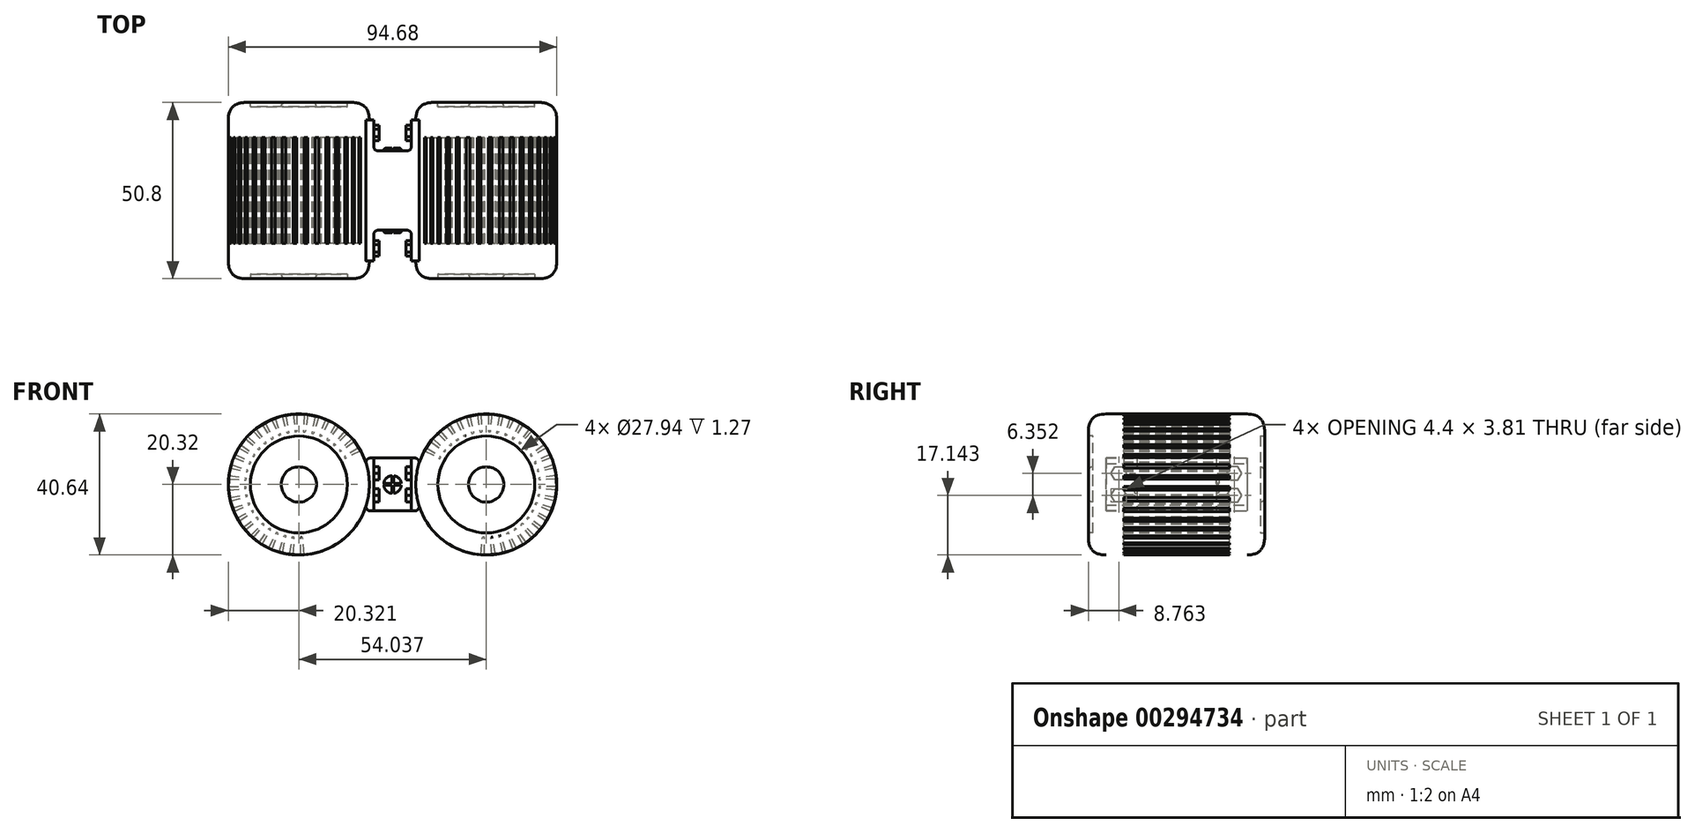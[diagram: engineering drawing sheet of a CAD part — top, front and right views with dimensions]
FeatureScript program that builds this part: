
annotation { "Feature Type Name" : "Feature", "Feature Type Description" : "" }
export const myFeature = defineFeature(function(context is Context, id is Id, definition is map)
    precondition{}
    {
        {
            var Q0;
            Q0=qCreatedBy(makeId("Front.planeOp"),FACE);
            var sketch = newSketch(context, id + "F0", { "sketchPlane" : qUnion([Q0])});
            skArc(sketch, "E0", {"start": v(26.53, 38.5) * mm, "mid": v(31.42, 78.66) * mm, "end": v(18.88, 40.2) * mm});
            skCircle(sketch, "E1", {"center": v(-27.02, 58.82) * mm, "radius": 20.32 * mm});
            skArc(sketch, "E2", {"start": v(18.88, 40.2) * mm, "mid": v(22.62, 38.98) * mm, "end": v(26.53, 38.5) * mm});
            skSolve(sketch);
        }
        {
            var Q0;
            Q0=qSketchRegion(id+"F0",true);
            extrude(context, id + "F1", {"entities" : qUnion([Q0]), "endBound" : BoundingType.SYMMETRIC, "depth" : 50.8 * mm});
        }
        {
            var Q0;
            Q0=qCreatedBy(makeId("Front.planeOp"),FACE);
            var sketch = newSketch(context, id + "F2", { "sketchPlane" : qUnion([Q0])});
            skLineSegment(sketch, "E3.1.0", {"start": v(13.83, 74.28) * mm, "end": v(17.03, 70.33) * mm});
            skLineSegment(sketch, "E3.1.1", {"start": v(13.07, 73.6) * mm, "end": v(16.65, 69.99) * mm});
            skLineSegment(sketch, "E3.1.2", {"start": v(13.07, 73.6) * mm, "end": v(13.83, 74.28) * mm});
            skLineSegment(sketch, "E3.1.3", {"start": v(16.65, 69.99) * mm, "end": v(17.03, 70.33) * mm, "construction": true});
            skLineSegment(sketch, "E3.1.4", {"start": v(16.65, 69.99) * mm, "end": v(17.03, 70.33) * mm});
            skPoint(sketch, "E4", {"position": v(27.02, 58.82) * mm});
            skPoint(sketch, "E5", {"position": v(-27.02, 58.82) * mm});
            skLineSegment(sketch, "E6", {"start": v(27.02, 58.82) * mm, "end": v(13.45, 73.94) * mm, "construction": true});
            skLineSegment(sketch, "E7.1.0", {"start": v(-13.07, 73.6) * mm, "end": v(-16.65, 69.99) * mm});
            skLineSegment(sketch, "E7.1.1", {"start": v(-13.83, 74.28) * mm, "end": v(-17.03, 70.33) * mm});
            skLineSegment(sketch, "E7.1.2", {"start": v(-13.83, 74.28) * mm, "end": v(-13.07, 73.6) * mm});
            skLineSegment(sketch, "E7.1.3", {"start": v(-17.03, 70.33) * mm, "end": v(-16.65, 69.99) * mm, "construction": true});
            skLineSegment(sketch, "E7.1.4", {"start": v(-17.03, 70.33) * mm, "end": v(-16.65, 69.99) * mm});
            skLineSegment(sketch, "E8", {"start": v(-27.02, 58.82) * mm, "end": v(-13.45, 73.94) * mm, "construction": true});
            skLineSegment(sketch, "E9.1.0", {"start": v(11.57, 72.03) * mm, "end": v(15.35, 68.63) * mm});
            skLineSegment(sketch, "E9.1.1", {"start": v(10.93, 71.24) * mm, "end": v(15.03, 68.23) * mm});
            skLineSegment(sketch, "E9.1.2", {"start": v(10.93, 71.24) * mm, "end": v(11.57, 72.03) * mm});
            skLineSegment(sketch, "E9.1.3", {"start": v(15.03, 68.23) * mm, "end": v(15.35, 68.63) * mm, "construction": true});
            skLineSegment(sketch, "E9.1.4", {"start": v(15.03, 68.23) * mm, "end": v(15.35, 68.63) * mm});
            skLineSegment(sketch, "E9.2.0", {"start": v(9.7, 69.45) * mm, "end": v(13.96, 66.68) * mm});
            skLineSegment(sketch, "E9.2.1", {"start": v(9.18, 68.57) * mm, "end": v(13.7, 66.24) * mm});
            skLineSegment(sketch, "E9.2.2", {"start": v(9.18, 68.57) * mm, "end": v(9.7, 69.45) * mm});
            skLineSegment(sketch, "E9.2.3", {"start": v(13.7, 66.24) * mm, "end": v(13.96, 66.68) * mm, "construction": true});
            skLineSegment(sketch, "E9.2.4", {"start": v(13.7, 66.24) * mm, "end": v(13.96, 66.68) * mm});
            skLineSegment(sketch, "E9.15.0", {"start": v(25.41, 38.55) * mm, "end": v(25.94, 43.62) * mm});
            skLineSegment(sketch, "E9.15.1", {"start": v(26.43, 38.5) * mm, "end": v(26.45, 43.59) * mm});
            skLineSegment(sketch, "E9.15.2", {"start": v(26.43, 38.5) * mm, "end": v(25.41, 38.55) * mm});
            skLineSegment(sketch, "E9.15.3", {"start": v(26.45, 43.59) * mm, "end": v(25.94, 43.62) * mm, "construction": true});
            skLineSegment(sketch, "E9.15.4", {"start": v(26.45, 43.59) * mm, "end": v(25.94, 43.62) * mm});
            skLineSegment(sketch, "E9.16.0", {"start": v(28.6, 38.55) * mm, "end": v(28.33, 43.63) * mm});
            skLineSegment(sketch, "E9.16.1", {"start": v(29.61, 38.66) * mm, "end": v(28.84, 43.69) * mm});
            skLineSegment(sketch, "E9.16.2", {"start": v(29.61, 38.66) * mm, "end": v(28.6, 38.55) * mm});
            skLineSegment(sketch, "E9.16.3", {"start": v(28.84, 43.69) * mm, "end": v(28.33, 43.63) * mm, "construction": true});
            skLineSegment(sketch, "E9.16.4", {"start": v(28.84, 43.69) * mm, "end": v(28.33, 43.63) * mm});
            skLineSegment(sketch, "E9.17.0", {"start": v(31.75, 39.05) * mm, "end": v(30.7, 44.03) * mm});
            skLineSegment(sketch, "E9.17.1", {"start": v(32.73, 39.31) * mm, "end": v(31.18, 44.16) * mm});
            skLineSegment(sketch, "E9.17.2", {"start": v(32.73, 39.31) * mm, "end": v(31.75, 39.05) * mm});
            skLineSegment(sketch, "E9.17.3", {"start": v(31.18, 44.16) * mm, "end": v(30.7, 44.03) * mm, "construction": true});
            skLineSegment(sketch, "E9.17.4", {"start": v(31.18, 44.16) * mm, "end": v(30.7, 44.03) * mm});
            skLineSegment(sketch, "E9.18.0", {"start": v(34.79, 40.03) * mm, "end": v(32.96, 44.78) * mm});
            skLineSegment(sketch, "E9.18.1", {"start": v(35.72, 40.45) * mm, "end": v(33.42, 44.99) * mm});
            skLineSegment(sketch, "E9.18.2", {"start": v(35.72, 40.45) * mm, "end": v(34.79, 40.03) * mm});
            skLineSegment(sketch, "E9.18.3", {"start": v(33.42, 44.99) * mm, "end": v(32.96, 44.78) * mm, "construction": true});
            skLineSegment(sketch, "E9.18.4", {"start": v(33.42, 44.99) * mm, "end": v(32.96, 44.78) * mm});
            skLineSegment(sketch, "E9.19.0", {"start": v(37.63, 41.48) * mm, "end": v(35.08, 45.89) * mm});
            skLineSegment(sketch, "E9.19.1", {"start": v(38.48, 42.03) * mm, "end": v(35.5, 46.16) * mm});
            skLineSegment(sketch, "E9.19.2", {"start": v(38.48, 42.03) * mm, "end": v(37.63, 41.48) * mm});
            skLineSegment(sketch, "E9.19.3", {"start": v(35.5, 46.16) * mm, "end": v(35.08, 45.89) * mm, "construction": true});
            skLineSegment(sketch, "E9.19.4", {"start": v(35.5, 46.16) * mm, "end": v(35.08, 45.89) * mm});
            skLineSegment(sketch, "E9.20.0", {"start": v(40.21, 43.35) * mm, "end": v(37, 47.3) * mm});
            skLineSegment(sketch, "E9.20.1", {"start": v(40.97, 44.03) * mm, "end": v(37.38, 47.65) * mm});
            skLineSegment(sketch, "E9.20.2", {"start": v(40.97, 44.03) * mm, "end": v(40.21, 43.35) * mm});
            skLineSegment(sketch, "E9.20.3", {"start": v(37.38, 47.65) * mm, "end": v(37, 47.3) * mm, "construction": true});
            skLineSegment(sketch, "E9.20.4", {"start": v(37.38, 47.65) * mm, "end": v(37, 47.3) * mm});
            skLineSegment(sketch, "E9.21.0", {"start": v(42.47, 45.6) * mm, "end": v(38.68, 49.01) * mm});
            skLineSegment(sketch, "E9.21.1", {"start": v(43.1, 46.4) * mm, "end": v(39, 49.4) * mm});
            skLineSegment(sketch, "E9.21.2", {"start": v(43.1, 46.4) * mm, "end": v(42.47, 45.6) * mm});
            skLineSegment(sketch, "E9.21.3", {"start": v(39, 49.4) * mm, "end": v(38.68, 49.01) * mm, "construction": true});
            skLineSegment(sketch, "E9.21.4", {"start": v(39, 49.4) * mm, "end": v(38.68, 49.01) * mm});
            skLineSegment(sketch, "E9.22.0", {"start": v(44.34, 48.19) * mm, "end": v(40.07, 50.96) * mm});
            skLineSegment(sketch, "E9.22.1", {"start": v(44.85, 49.07) * mm, "end": v(40.33, 51.4) * mm});
            skLineSegment(sketch, "E9.22.2", {"start": v(44.85, 49.07) * mm, "end": v(44.34, 48.19) * mm});
            skLineSegment(sketch, "E9.22.3", {"start": v(40.33, 51.4) * mm, "end": v(40.07, 50.96) * mm, "construction": true});
            skLineSegment(sketch, "E9.22.4", {"start": v(40.33, 51.4) * mm, "end": v(40.07, 50.96) * mm});
            skLineSegment(sketch, "E9.23.0", {"start": v(45.8, 51.03) * mm, "end": v(41.14, 53.1) * mm});
            skLineSegment(sketch, "E9.23.1", {"start": v(46.16, 51.98) * mm, "end": v(41.33, 53.57) * mm});
            skLineSegment(sketch, "E9.23.2", {"start": v(46.16, 51.98) * mm, "end": v(45.8, 51.03) * mm});
            skLineSegment(sketch, "E9.23.3", {"start": v(41.33, 53.57) * mm, "end": v(41.14, 53.1) * mm, "construction": true});
            skLineSegment(sketch, "E9.23.4", {"start": v(41.33, 53.57) * mm, "end": v(41.14, 53.1) * mm});
            skLineSegment(sketch, "E9.24.0", {"start": v(46.78, 54.06) * mm, "end": v(41.86, 55.37) * mm});
            skLineSegment(sketch, "E9.24.1", {"start": v(47, 55.05) * mm, "end": v(41.97, 55.87) * mm});
            skLineSegment(sketch, "E9.24.2", {"start": v(47, 55.05) * mm, "end": v(46.78, 54.06) * mm});
            skLineSegment(sketch, "E9.24.3", {"start": v(41.97, 55.87) * mm, "end": v(41.86, 55.37) * mm, "construction": true});
            skLineSegment(sketch, "E9.24.4", {"start": v(41.97, 55.87) * mm, "end": v(41.86, 55.37) * mm});
            skLineSegment(sketch, "E9.25.0", {"start": v(47.28, 57.21) * mm, "end": v(42.22, 57.74) * mm});
            skLineSegment(sketch, "E9.25.1", {"start": v(47.34, 58.23) * mm, "end": v(42.25, 58.25) * mm});
            skLineSegment(sketch, "E9.25.2", {"start": v(47.34, 58.23) * mm, "end": v(47.28, 57.21) * mm});
            skLineSegment(sketch, "E9.25.3", {"start": v(42.25, 58.25) * mm, "end": v(42.22, 57.74) * mm, "construction": true});
            skLineSegment(sketch, "E9.25.4", {"start": v(42.25, 58.25) * mm, "end": v(42.22, 57.74) * mm});
            skLineSegment(sketch, "E9.26.0", {"start": v(47.28, 60.4) * mm, "end": v(42.2, 60.13) * mm});
            skLineSegment(sketch, "E9.26.1", {"start": v(47.18, 61.41) * mm, "end": v(42.15, 60.64) * mm});
            skLineSegment(sketch, "E9.26.2", {"start": v(47.18, 61.41) * mm, "end": v(47.28, 60.4) * mm});
            skLineSegment(sketch, "E9.26.3", {"start": v(42.15, 60.64) * mm, "end": v(42.2, 60.13) * mm, "construction": true});
            skLineSegment(sketch, "E9.26.4", {"start": v(42.15, 60.64) * mm, "end": v(42.2, 60.13) * mm});
            skLineSegment(sketch, "E9.27.0", {"start": v(46.79, 63.55) * mm, "end": v(41.8, 62.5) * mm});
            skLineSegment(sketch, "E9.27.1", {"start": v(46.52, 64.53) * mm, "end": v(41.68, 62.98) * mm});
            skLineSegment(sketch, "E9.27.2", {"start": v(46.52, 64.53) * mm, "end": v(46.79, 63.55) * mm});
            skLineSegment(sketch, "E9.27.3", {"start": v(41.68, 62.98) * mm, "end": v(41.8, 62.5) * mm, "construction": true});
            skLineSegment(sketch, "E9.27.4", {"start": v(41.68, 62.98) * mm, "end": v(41.8, 62.5) * mm});
            skLineSegment(sketch, "E9.28.0", {"start": v(45.8, 66.59) * mm, "end": v(41.05, 64.76) * mm});
            skLineSegment(sketch, "E9.28.1", {"start": v(45.4, 67.51) * mm, "end": v(40.85, 65.22) * mm});
            skLineSegment(sketch, "E9.28.2", {"start": v(45.4, 67.51) * mm, "end": v(45.8, 66.59) * mm});
            skLineSegment(sketch, "E9.28.3", {"start": v(40.85, 65.22) * mm, "end": v(41.05, 64.76) * mm, "construction": true});
            skLineSegment(sketch, "E9.28.4", {"start": v(40.85, 65.22) * mm, "end": v(41.05, 64.76) * mm});
            skLineSegment(sketch, "E9.29.0", {"start": v(44.36, 69.43) * mm, "end": v(39.95, 66.88) * mm});
            skLineSegment(sketch, "E9.29.1", {"start": v(43.8, 70.28) * mm, "end": v(39.67, 67.3) * mm});
            skLineSegment(sketch, "E9.29.2", {"start": v(43.8, 70.28) * mm, "end": v(44.36, 69.43) * mm});
            skLineSegment(sketch, "E9.29.3", {"start": v(39.67, 67.3) * mm, "end": v(39.95, 66.88) * mm, "construction": true});
            skLineSegment(sketch, "E9.29.4", {"start": v(39.67, 67.3) * mm, "end": v(39.95, 66.88) * mm});
            skLineSegment(sketch, "E9.30.0", {"start": v(42.48, 72) * mm, "end": v(38.53, 68.8) * mm});
            skLineSegment(sketch, "E9.30.1", {"start": v(41.8, 72.77) * mm, "end": v(38.2, 69.18) * mm});
            skLineSegment(sketch, "E9.30.2", {"start": v(41.8, 72.77) * mm, "end": v(42.48, 72) * mm});
            skLineSegment(sketch, "E9.30.3", {"start": v(38.2, 69.18) * mm, "end": v(38.53, 68.8) * mm, "construction": true});
            skLineSegment(sketch, "E9.30.4", {"start": v(38.2, 69.18) * mm, "end": v(38.53, 68.8) * mm});
            skLineSegment(sketch, "E9.31.0", {"start": v(40.23, 74.27) * mm, "end": v(36.83, 70.48) * mm});
            skLineSegment(sketch, "E9.31.1", {"start": v(39.44, 74.9) * mm, "end": v(36.43, 70.8) * mm});
            skLineSegment(sketch, "E9.31.2", {"start": v(39.44, 74.9) * mm, "end": v(40.23, 74.27) * mm});
            skLineSegment(sketch, "E9.31.3", {"start": v(36.43, 70.8) * mm, "end": v(36.83, 70.48) * mm, "construction": true});
            skLineSegment(sketch, "E9.31.4", {"start": v(36.43, 70.8) * mm, "end": v(36.83, 70.48) * mm});
            skLineSegment(sketch, "E9.32.0", {"start": v(37.65, 76.14) * mm, "end": v(34.88, 71.87) * mm});
            skLineSegment(sketch, "E9.32.1", {"start": v(36.77, 76.65) * mm, "end": v(34.44, 72.13) * mm});
            skLineSegment(sketch, "E9.32.2", {"start": v(36.77, 76.65) * mm, "end": v(37.65, 76.14) * mm});
            skLineSegment(sketch, "E9.32.3", {"start": v(34.44, 72.13) * mm, "end": v(34.88, 71.87) * mm, "construction": true});
            skLineSegment(sketch, "E9.32.4", {"start": v(34.44, 72.13) * mm, "end": v(34.88, 71.87) * mm});
            skLineSegment(sketch, "E9.33.0", {"start": v(34.8, 77.6) * mm, "end": v(32.74, 72.94) * mm});
            skLineSegment(sketch, "E9.33.1", {"start": v(33.86, 77.96) * mm, "end": v(32.27, 73.13) * mm});
            skLineSegment(sketch, "E9.33.2", {"start": v(33.86, 77.96) * mm, "end": v(34.8, 77.6) * mm});
            skLineSegment(sketch, "E9.33.3", {"start": v(32.27, 73.13) * mm, "end": v(32.74, 72.94) * mm, "construction": true});
            skLineSegment(sketch, "E9.33.4", {"start": v(32.27, 73.13) * mm, "end": v(32.74, 72.94) * mm});
            skLineSegment(sketch, "E9.34.0", {"start": v(31.78, 78.58) * mm, "end": v(30.46, 73.66) * mm});
            skLineSegment(sketch, "E9.34.1", {"start": v(30.78, 78.8) * mm, "end": v(29.96, 73.77) * mm});
            skLineSegment(sketch, "E9.34.2", {"start": v(30.78, 78.8) * mm, "end": v(31.78, 78.58) * mm});
            skLineSegment(sketch, "E9.34.3", {"start": v(29.96, 73.77) * mm, "end": v(30.46, 73.66) * mm, "construction": true});
            skLineSegment(sketch, "E9.34.4", {"start": v(29.96, 73.77) * mm, "end": v(30.46, 73.66) * mm});
            skLineSegment(sketch, "E9.35.0", {"start": v(28.63, 79.08) * mm, "end": v(28.1, 74.02) * mm});
            skLineSegment(sketch, "E9.35.1", {"start": v(27.61, 79.14) * mm, "end": v(27.59, 74.05) * mm});
            skLineSegment(sketch, "E9.35.2", {"start": v(27.61, 79.14) * mm, "end": v(28.63, 79.08) * mm});
            skLineSegment(sketch, "E9.35.3", {"start": v(27.59, 74.05) * mm, "end": v(28.1, 74.02) * mm, "construction": true});
            skLineSegment(sketch, "E9.35.4", {"start": v(27.59, 74.05) * mm, "end": v(28.1, 74.02) * mm});
            skLineSegment(sketch, "E9.36.0", {"start": v(25.44, 79.08) * mm, "end": v(25.7, 74) * mm});
            skLineSegment(sketch, "E9.36.1", {"start": v(24.42, 78.98) * mm, "end": v(25.2, 73.95) * mm});
            skLineSegment(sketch, "E9.36.2", {"start": v(24.42, 78.98) * mm, "end": v(25.44, 79.08) * mm});
            skLineSegment(sketch, "E9.36.3", {"start": v(25.2, 73.95) * mm, "end": v(25.7, 74) * mm, "construction": true});
            skLineSegment(sketch, "E9.36.4", {"start": v(25.2, 73.95) * mm, "end": v(25.7, 74) * mm});
            skLineSegment(sketch, "E9.37.0", {"start": v(22.28, 78.59) * mm, "end": v(23.35, 73.6) * mm});
            skLineSegment(sketch, "E9.37.1", {"start": v(21.3, 78.32) * mm, "end": v(22.86, 73.48) * mm});
            skLineSegment(sketch, "E9.37.2", {"start": v(21.3, 78.32) * mm, "end": v(22.28, 78.59) * mm});
            skLineSegment(sketch, "E9.37.3", {"start": v(22.86, 73.48) * mm, "end": v(23.35, 73.6) * mm, "construction": true});
            skLineSegment(sketch, "E9.37.4", {"start": v(22.86, 73.48) * mm, "end": v(23.35, 73.6) * mm});
            skLineSegment(sketch, "E9.38.0", {"start": v(19.25, 77.6) * mm, "end": v(21.08, 72.85) * mm});
            skLineSegment(sketch, "E9.38.1", {"start": v(18.32, 77.19) * mm, "end": v(20.61, 72.65) * mm});
            skLineSegment(sketch, "E9.38.2", {"start": v(18.32, 77.19) * mm, "end": v(19.25, 77.6) * mm});
            skLineSegment(sketch, "E9.38.3", {"start": v(20.61, 72.65) * mm, "end": v(21.08, 72.85) * mm, "construction": true});
            skLineSegment(sketch, "E9.38.4", {"start": v(20.61, 72.65) * mm, "end": v(21.08, 72.85) * mm});
            skLineSegment(sketch, "E9.39.0", {"start": v(16.4, 76.15) * mm, "end": v(18.96, 71.75) * mm});
            skLineSegment(sketch, "E9.39.1", {"start": v(15.56, 75.6) * mm, "end": v(18.53, 71.47) * mm});
            skLineSegment(sketch, "E9.39.2", {"start": v(15.56, 75.6) * mm, "end": v(16.4, 76.15) * mm});
            skLineSegment(sketch, "E9.39.3", {"start": v(18.53, 71.47) * mm, "end": v(18.96, 71.75) * mm, "construction": true});
            skLineSegment(sketch, "E9.39.4", {"start": v(18.53, 71.47) * mm, "end": v(18.96, 71.75) * mm});
            skLineSegment(sketch, "E10.1.0", {"start": v(-15.56, 75.6) * mm, "end": v(-18.53, 71.47) * mm});
            skLineSegment(sketch, "E10.1.1", {"start": v(-16.4, 76.15) * mm, "end": v(-18.96, 71.75) * mm});
            skLineSegment(sketch, "E10.1.2", {"start": v(-16.4, 76.15) * mm, "end": v(-15.56, 75.6) * mm});
            skLineSegment(sketch, "E10.1.3", {"start": v(-18.96, 71.75) * mm, "end": v(-18.53, 71.47) * mm, "construction": true});
            skLineSegment(sketch, "E10.1.4", {"start": v(-18.96, 71.75) * mm, "end": v(-18.53, 71.47) * mm});
            skLineSegment(sketch, "E10.2.0", {"start": v(-18.32, 77.19) * mm, "end": v(-20.61, 72.65) * mm});
            skLineSegment(sketch, "E10.2.1", {"start": v(-19.25, 77.6) * mm, "end": v(-21.08, 72.85) * mm});
            skLineSegment(sketch, "E10.2.2", {"start": v(-19.25, 77.6) * mm, "end": v(-18.32, 77.19) * mm});
            skLineSegment(sketch, "E10.2.3", {"start": v(-21.08, 72.85) * mm, "end": v(-20.61, 72.65) * mm, "construction": true});
            skLineSegment(sketch, "E10.2.4", {"start": v(-21.08, 72.85) * mm, "end": v(-20.61, 72.65) * mm});
            skLineSegment(sketch, "E10.3.0", {"start": v(-21.3, 78.32) * mm, "end": v(-22.86, 73.48) * mm});
            skLineSegment(sketch, "E10.3.1", {"start": v(-22.28, 78.59) * mm, "end": v(-23.35, 73.6) * mm});
            skLineSegment(sketch, "E10.3.2", {"start": v(-22.28, 78.59) * mm, "end": v(-21.3, 78.32) * mm});
            skLineSegment(sketch, "E10.3.3", {"start": v(-23.35, 73.6) * mm, "end": v(-22.86, 73.48) * mm, "construction": true});
            skLineSegment(sketch, "E10.3.4", {"start": v(-23.35, 73.6) * mm, "end": v(-22.86, 73.48) * mm});
            skLineSegment(sketch, "E10.4.0", {"start": v(-24.42, 78.98) * mm, "end": v(-25.2, 73.95) * mm});
            skLineSegment(sketch, "E10.4.1", {"start": v(-25.44, 79.08) * mm, "end": v(-25.7, 74) * mm});
            skLineSegment(sketch, "E10.4.2", {"start": v(-25.44, 79.08) * mm, "end": v(-24.42, 78.98) * mm});
            skLineSegment(sketch, "E10.4.3", {"start": v(-25.7, 74) * mm, "end": v(-25.2, 73.95) * mm, "construction": true});
            skLineSegment(sketch, "E10.4.4", {"start": v(-25.7, 74) * mm, "end": v(-25.2, 73.95) * mm});
            skLineSegment(sketch, "E10.5.0", {"start": v(-27.61, 79.14) * mm, "end": v(-27.59, 74.05) * mm});
            skLineSegment(sketch, "E10.5.1", {"start": v(-28.63, 79.08) * mm, "end": v(-28.1, 74.02) * mm});
            skLineSegment(sketch, "E10.5.2", {"start": v(-28.63, 79.08) * mm, "end": v(-27.61, 79.14) * mm});
            skLineSegment(sketch, "E10.5.3", {"start": v(-28.1, 74.02) * mm, "end": v(-27.59, 74.05) * mm, "construction": true});
            skLineSegment(sketch, "E10.5.4", {"start": v(-28.1, 74.02) * mm, "end": v(-27.59, 74.05) * mm});
            skLineSegment(sketch, "E10.6.0", {"start": v(-30.78, 78.8) * mm, "end": v(-29.96, 73.77) * mm});
            skLineSegment(sketch, "E10.6.1", {"start": v(-31.78, 78.58) * mm, "end": v(-30.46, 73.66) * mm});
            skLineSegment(sketch, "E10.6.2", {"start": v(-31.78, 78.58) * mm, "end": v(-30.78, 78.8) * mm});
            skLineSegment(sketch, "E10.6.3", {"start": v(-30.46, 73.66) * mm, "end": v(-29.96, 73.77) * mm, "construction": true});
            skLineSegment(sketch, "E10.6.4", {"start": v(-30.46, 73.66) * mm, "end": v(-29.96, 73.77) * mm});
            skLineSegment(sketch, "E10.7.0", {"start": v(-33.86, 77.96) * mm, "end": v(-32.27, 73.13) * mm});
            skLineSegment(sketch, "E10.7.1", {"start": v(-34.8, 77.6) * mm, "end": v(-32.74, 72.94) * mm});
            skLineSegment(sketch, "E10.7.2", {"start": v(-34.8, 77.6) * mm, "end": v(-33.86, 77.96) * mm});
            skLineSegment(sketch, "E10.7.3", {"start": v(-32.74, 72.94) * mm, "end": v(-32.27, 73.13) * mm, "construction": true});
            skLineSegment(sketch, "E10.7.4", {"start": v(-32.74, 72.94) * mm, "end": v(-32.27, 73.13) * mm});
            skLineSegment(sketch, "E10.8.0", {"start": v(-36.77, 76.65) * mm, "end": v(-34.44, 72.13) * mm});
            skLineSegment(sketch, "E10.8.1", {"start": v(-37.65, 76.14) * mm, "end": v(-34.88, 71.87) * mm});
            skLineSegment(sketch, "E10.8.2", {"start": v(-37.65, 76.14) * mm, "end": v(-36.77, 76.65) * mm});
            skLineSegment(sketch, "E10.8.3", {"start": v(-34.88, 71.87) * mm, "end": v(-34.44, 72.13) * mm, "construction": true});
            skLineSegment(sketch, "E10.8.4", {"start": v(-34.88, 71.87) * mm, "end": v(-34.44, 72.13) * mm});
            skLineSegment(sketch, "E10.9.0", {"start": v(-39.44, 74.9) * mm, "end": v(-36.43, 70.8) * mm});
            skLineSegment(sketch, "E10.9.1", {"start": v(-40.23, 74.27) * mm, "end": v(-36.83, 70.48) * mm});
            skLineSegment(sketch, "E10.9.2", {"start": v(-40.23, 74.27) * mm, "end": v(-39.44, 74.9) * mm});
            skLineSegment(sketch, "E10.9.3", {"start": v(-36.83, 70.48) * mm, "end": v(-36.43, 70.8) * mm, "construction": true});
            skLineSegment(sketch, "E10.9.4", {"start": v(-36.83, 70.48) * mm, "end": v(-36.43, 70.8) * mm});
            skLineSegment(sketch, "E10.10.0", {"start": v(-41.8, 72.77) * mm, "end": v(-38.2, 69.18) * mm});
            skLineSegment(sketch, "E10.10.1", {"start": v(-42.48, 72) * mm, "end": v(-38.53, 68.8) * mm});
            skLineSegment(sketch, "E10.10.2", {"start": v(-42.48, 72) * mm, "end": v(-41.8, 72.77) * mm});
            skLineSegment(sketch, "E10.10.3", {"start": v(-38.53, 68.8) * mm, "end": v(-38.2, 69.18) * mm, "construction": true});
            skLineSegment(sketch, "E10.10.4", {"start": v(-38.53, 68.8) * mm, "end": v(-38.2, 69.18) * mm});
            skLineSegment(sketch, "E10.11.0", {"start": v(-43.8, 70.28) * mm, "end": v(-39.67, 67.3) * mm});
            skLineSegment(sketch, "E10.11.1", {"start": v(-44.36, 69.43) * mm, "end": v(-39.95, 66.88) * mm});
            skLineSegment(sketch, "E10.11.2", {"start": v(-44.36, 69.43) * mm, "end": v(-43.8, 70.28) * mm});
            skLineSegment(sketch, "E10.11.3", {"start": v(-39.95, 66.88) * mm, "end": v(-39.67, 67.3) * mm, "construction": true});
            skLineSegment(sketch, "E10.11.4", {"start": v(-39.95, 66.88) * mm, "end": v(-39.67, 67.3) * mm});
            skLineSegment(sketch, "E10.12.0", {"start": v(-45.4, 67.51) * mm, "end": v(-40.85, 65.22) * mm});
            skLineSegment(sketch, "E10.12.1", {"start": v(-45.8, 66.59) * mm, "end": v(-41.05, 64.76) * mm});
            skLineSegment(sketch, "E10.12.2", {"start": v(-45.8, 66.59) * mm, "end": v(-45.4, 67.51) * mm});
            skLineSegment(sketch, "E10.12.3", {"start": v(-41.05, 64.76) * mm, "end": v(-40.85, 65.22) * mm, "construction": true});
            skLineSegment(sketch, "E10.12.4", {"start": v(-41.05, 64.76) * mm, "end": v(-40.85, 65.22) * mm});
            skLineSegment(sketch, "E10.13.0", {"start": v(-46.52, 64.53) * mm, "end": v(-41.68, 62.98) * mm});
            skLineSegment(sketch, "E10.13.1", {"start": v(-46.79, 63.55) * mm, "end": v(-41.8, 62.5) * mm});
            skLineSegment(sketch, "E10.13.2", {"start": v(-46.79, 63.55) * mm, "end": v(-46.52, 64.53) * mm});
            skLineSegment(sketch, "E10.13.3", {"start": v(-41.8, 62.5) * mm, "end": v(-41.68, 62.98) * mm, "construction": true});
            skLineSegment(sketch, "E10.13.4", {"start": v(-41.8, 62.5) * mm, "end": v(-41.68, 62.98) * mm});
            skLineSegment(sketch, "E10.14.0", {"start": v(-47.18, 61.41) * mm, "end": v(-42.15, 60.64) * mm});
            skLineSegment(sketch, "E10.14.1", {"start": v(-47.28, 60.4) * mm, "end": v(-42.2, 60.13) * mm});
            skLineSegment(sketch, "E10.14.2", {"start": v(-47.28, 60.4) * mm, "end": v(-47.18, 61.41) * mm});
            skLineSegment(sketch, "E10.14.3", {"start": v(-42.2, 60.13) * mm, "end": v(-42.15, 60.64) * mm, "construction": true});
            skLineSegment(sketch, "E10.14.4", {"start": v(-42.2, 60.13) * mm, "end": v(-42.15, 60.64) * mm});
            skLineSegment(sketch, "E10.15.0", {"start": v(-47.34, 58.23) * mm, "end": v(-42.25, 58.25) * mm});
            skLineSegment(sketch, "E10.15.1", {"start": v(-47.28, 57.21) * mm, "end": v(-42.22, 57.74) * mm});
            skLineSegment(sketch, "E10.15.2", {"start": v(-47.28, 57.21) * mm, "end": v(-47.34, 58.23) * mm});
            skLineSegment(sketch, "E10.15.3", {"start": v(-42.22, 57.74) * mm, "end": v(-42.25, 58.25) * mm, "construction": true});
            skLineSegment(sketch, "E10.15.4", {"start": v(-42.22, 57.74) * mm, "end": v(-42.25, 58.25) * mm});
            skLineSegment(sketch, "E10.16.0", {"start": v(-47, 55.05) * mm, "end": v(-41.97, 55.87) * mm});
            skLineSegment(sketch, "E10.16.1", {"start": v(-46.78, 54.06) * mm, "end": v(-41.86, 55.37) * mm});
            skLineSegment(sketch, "E10.16.2", {"start": v(-46.78, 54.06) * mm, "end": v(-47, 55.05) * mm});
            skLineSegment(sketch, "E10.16.3", {"start": v(-41.86, 55.37) * mm, "end": v(-41.97, 55.87) * mm, "construction": true});
            skLineSegment(sketch, "E10.16.4", {"start": v(-41.86, 55.37) * mm, "end": v(-41.97, 55.87) * mm});
            skLineSegment(sketch, "E10.17.0", {"start": v(-46.16, 51.98) * mm, "end": v(-41.33, 53.57) * mm});
            skLineSegment(sketch, "E10.17.1", {"start": v(-45.8, 51.03) * mm, "end": v(-41.14, 53.1) * mm});
            skLineSegment(sketch, "E10.17.2", {"start": v(-45.8, 51.03) * mm, "end": v(-46.16, 51.98) * mm});
            skLineSegment(sketch, "E10.17.3", {"start": v(-41.14, 53.1) * mm, "end": v(-41.33, 53.57) * mm, "construction": true});
            skLineSegment(sketch, "E10.17.4", {"start": v(-41.14, 53.1) * mm, "end": v(-41.33, 53.57) * mm});
            skLineSegment(sketch, "E10.18.0", {"start": v(-44.85, 49.07) * mm, "end": v(-40.33, 51.4) * mm});
            skLineSegment(sketch, "E10.18.1", {"start": v(-44.34, 48.19) * mm, "end": v(-40.07, 50.96) * mm});
            skLineSegment(sketch, "E10.18.2", {"start": v(-44.34, 48.19) * mm, "end": v(-44.85, 49.07) * mm});
            skLineSegment(sketch, "E10.18.3", {"start": v(-40.07, 50.96) * mm, "end": v(-40.33, 51.4) * mm, "construction": true});
            skLineSegment(sketch, "E10.18.4", {"start": v(-40.07, 50.96) * mm, "end": v(-40.33, 51.4) * mm});
            skLineSegment(sketch, "E10.19.0", {"start": v(-43.1, 46.4) * mm, "end": v(-39, 49.4) * mm});
            skLineSegment(sketch, "E10.19.1", {"start": v(-42.47, 45.6) * mm, "end": v(-38.68, 49.01) * mm});
            skLineSegment(sketch, "E10.19.2", {"start": v(-42.47, 45.6) * mm, "end": v(-43.1, 46.4) * mm});
            skLineSegment(sketch, "E10.19.3", {"start": v(-38.68, 49.01) * mm, "end": v(-39, 49.4) * mm, "construction": true});
            skLineSegment(sketch, "E10.19.4", {"start": v(-38.68, 49.01) * mm, "end": v(-39, 49.4) * mm});
            skLineSegment(sketch, "E10.20.0", {"start": v(-40.97, 44.03) * mm, "end": v(-37.38, 47.65) * mm});
            skLineSegment(sketch, "E10.20.1", {"start": v(-40.21, 43.35) * mm, "end": v(-37, 47.3) * mm});
            skLineSegment(sketch, "E10.20.2", {"start": v(-40.21, 43.35) * mm, "end": v(-40.97, 44.03) * mm});
            skLineSegment(sketch, "E10.20.3", {"start": v(-37, 47.3) * mm, "end": v(-37.38, 47.65) * mm, "construction": true});
            skLineSegment(sketch, "E10.20.4", {"start": v(-37, 47.3) * mm, "end": v(-37.38, 47.65) * mm});
            skLineSegment(sketch, "E10.21.0", {"start": v(-38.48, 42.03) * mm, "end": v(-35.5, 46.16) * mm});
            skLineSegment(sketch, "E10.21.1", {"start": v(-37.63, 41.48) * mm, "end": v(-35.08, 45.89) * mm});
            skLineSegment(sketch, "E10.21.2", {"start": v(-37.63, 41.48) * mm, "end": v(-38.48, 42.03) * mm});
            skLineSegment(sketch, "E10.21.3", {"start": v(-35.08, 45.89) * mm, "end": v(-35.5, 46.16) * mm, "construction": true});
            skLineSegment(sketch, "E10.21.4", {"start": v(-35.08, 45.89) * mm, "end": v(-35.5, 46.16) * mm});
            skLineSegment(sketch, "E10.22.0", {"start": v(-35.72, 40.45) * mm, "end": v(-33.42, 44.99) * mm});
            skLineSegment(sketch, "E10.22.1", {"start": v(-34.79, 40.03) * mm, "end": v(-32.96, 44.78) * mm});
            skLineSegment(sketch, "E10.22.2", {"start": v(-34.79, 40.03) * mm, "end": v(-35.72, 40.45) * mm});
            skLineSegment(sketch, "E10.22.3", {"start": v(-32.96, 44.78) * mm, "end": v(-33.42, 44.99) * mm, "construction": true});
            skLineSegment(sketch, "E10.22.4", {"start": v(-32.96, 44.78) * mm, "end": v(-33.42, 44.99) * mm});
            skLineSegment(sketch, "E10.23.0", {"start": v(-32.73, 39.31) * mm, "end": v(-31.18, 44.16) * mm});
            skLineSegment(sketch, "E10.23.1", {"start": v(-31.75, 39.05) * mm, "end": v(-30.7, 44.03) * mm});
            skLineSegment(sketch, "E10.23.2", {"start": v(-31.75, 39.05) * mm, "end": v(-32.73, 39.31) * mm});
            skLineSegment(sketch, "E10.23.3", {"start": v(-30.7, 44.03) * mm, "end": v(-31.18, 44.16) * mm, "construction": true});
            skLineSegment(sketch, "E10.23.4", {"start": v(-30.7, 44.03) * mm, "end": v(-31.18, 44.16) * mm});
            skLineSegment(sketch, "E10.24.0", {"start": v(-29.61, 38.66) * mm, "end": v(-28.84, 43.69) * mm});
            skLineSegment(sketch, "E10.24.1", {"start": v(-28.6, 38.55) * mm, "end": v(-28.33, 43.63) * mm});
            skLineSegment(sketch, "E10.24.2", {"start": v(-28.6, 38.55) * mm, "end": v(-29.61, 38.66) * mm});
            skLineSegment(sketch, "E10.24.3", {"start": v(-28.33, 43.63) * mm, "end": v(-28.84, 43.69) * mm, "construction": true});
            skLineSegment(sketch, "E10.24.4", {"start": v(-28.33, 43.63) * mm, "end": v(-28.84, 43.69) * mm});
            skLineSegment(sketch, "E10.25.0", {"start": v(-26.43, 38.5) * mm, "end": v(-26.45, 43.59) * mm});
            skLineSegment(sketch, "E10.25.1", {"start": v(-25.41, 38.55) * mm, "end": v(-25.94, 43.62) * mm});
            skLineSegment(sketch, "E10.25.2", {"start": v(-25.41, 38.55) * mm, "end": v(-26.43, 38.5) * mm});
            skLineSegment(sketch, "E10.25.3", {"start": v(-25.94, 43.62) * mm, "end": v(-26.45, 43.59) * mm, "construction": true});
            skLineSegment(sketch, "E10.25.4", {"start": v(-25.94, 43.62) * mm, "end": v(-26.45, 43.59) * mm});
            skLineSegment(sketch, "E10.38.0", {"start": v(-9.18, 68.57) * mm, "end": v(-13.7, 66.24) * mm});
            skLineSegment(sketch, "E10.38.1", {"start": v(-9.7, 69.45) * mm, "end": v(-13.96, 66.68) * mm});
            skLineSegment(sketch, "E10.38.2", {"start": v(-9.7, 69.45) * mm, "end": v(-9.18, 68.57) * mm});
            skLineSegment(sketch, "E10.38.3", {"start": v(-13.96, 66.68) * mm, "end": v(-13.7, 66.24) * mm, "construction": true});
            skLineSegment(sketch, "E10.38.4", {"start": v(-13.96, 66.68) * mm, "end": v(-13.7, 66.24) * mm});
            skLineSegment(sketch, "E10.39.0", {"start": v(-10.93, 71.24) * mm, "end": v(-15.03, 68.23) * mm});
            skLineSegment(sketch, "E10.39.1", {"start": v(-11.57, 72.03) * mm, "end": v(-15.35, 68.63) * mm});
            skLineSegment(sketch, "E10.39.2", {"start": v(-11.57, 72.03) * mm, "end": v(-10.93, 71.24) * mm});
            skLineSegment(sketch, "E10.39.3", {"start": v(-15.35, 68.63) * mm, "end": v(-15.03, 68.23) * mm, "construction": true});
            skLineSegment(sketch, "E10.39.4", {"start": v(-15.35, 68.63) * mm, "end": v(-15.03, 68.23) * mm});
            skSolve(sketch);
        }
        {
            var Q0;
            Q0=qSketchRegion(id+"F2",true);
            extrude(context, id + "F3", {"entities" : qUnion([Q0]), "operationType" : NewBodyOperationType.REMOVE, "endBound" : BoundingType.SYMMETRIC, "oppositeDirection" : true, "depth" : 30.48 * mm});
        }
        {
            var Q0;
            Q0=makeQuery(id+"F1.opExtrude","CAP_EDGE",EDGE,{"disambiguationData":[OSD([sQuery(id+"F0.wireOp",EDGE,"E0")])],"isStart":false});
            var Q1;
            Q1=makeQuery(id+"F1.opExtrude","CAP_EDGE",EDGE,{"disambiguationData":[OSD([sQuery(id+"F0.wireOp",EDGE,"E0")])],"isStart":true});
            var Q2;
            Q2=makeQuery(id+"F1.opExtrude","CAP_EDGE",EDGE,{"disambiguationData":[OSD([sQuery(id+"F0.wireOp",EDGE,"eJ6pUaNj-pi6J-WJvS-oHvt-8XujmQXpYSx1")])],"isStart":true});
            var Q3;
            Q3=makeQuery(id+"F1.opExtrude","CAP_EDGE",EDGE,{"disambiguationData":[OSD([sQuery(id+"F0.wireOp",EDGE,"eJ6pUaNj-pi6J-WJvS-oHvt-8XujmQXpYSx1")])],"isStart":false});
            var Q4;
            Q4=makeQuery(id+"F1.opExtrude","CAP_EDGE",EDGE,{"disambiguationData":[OSD([sQuery(id+"F0.wireOp",EDGE,"E1")])],"isStart":false});
            var Q5;
            Q5=makeQuery(id+"F1.opExtrude","CAP_EDGE",EDGE,{"disambiguationData":[OSD([sQuery(id+"F0.wireOp",EDGE,"E1")])],"isStart":true});
            fillet(context, id + "F4", {"entities" : qUnion([Q0, Q1, Q2, Q3, Q4, Q5]), "radius" : 5.08 * mm, "tangentPropagation" : true, "rho" : 0.5, "crossSection" : FilletCrossSection.CONIC, "allowEdgeOverflow" : false});
        }
        {
            var Q0;
            Q0=makeQuery(id+"F1.opExtrude","CAP_FACE",FACE,{"disambiguationData":[OSD([sQuery(id+"F0.wireOp",EDGE,"E0"),sQuery(id+"F0.wireOp",EDGE,"E2")])],"isStart":false});
            var sketch = newSketch(context, id + "F5", { "sketchPlane" : qUnion([Q0])});
            skCircle(sketch, "E11", {"center": v(27.02, 58.82) * mm, "radius": 20.32 * mm, "construction": true});
            skCircle(sketch, "E12", {"center": v(-27.02, 58.82) * mm, "radius": 20.32 * mm, "construction": true});
            skCircle(sketch, "E13", {"center": v(-27.02, 58.82) * mm, "radius": 13.97 * mm});
            skCircle(sketch, "E14", {"center": v(27.02, 58.82) * mm, "radius": 13.97 * mm});
            skCircle(sketch, "E15", {"center": v(-27.02, 58.82) * mm, "radius": 5.08 * mm});
            skCircle(sketch, "E16", {"center": v(27.02, 58.82) * mm, "radius": 5.08 * mm});
            skSolve(sketch);
        }
        {
            var Q0;
            Q0=qSketchRegion(id+"F5",true);
            extrude(context, id + "F6", {"entities" : qUnion([Q0]), "operationType" : NewBodyOperationType.REMOVE, "oppositeDirection" : true, "depth" : 1.27 * mm});
        }
        {
            var Q0;
            Q0=makeQuery(id+"F1.opExtrude","CAP_FACE",FACE,{"disambiguationData":[OSD([sQuery(id+"F0.wireOp",EDGE,"E0"),sQuery(id+"F0.wireOp",EDGE,"E2")])],"isStart":true});
            var sketch = newSketch(context, id + "F7", { "sketchPlane" : qUnion([Q0])});
            skCircle(sketch, "E17", {"center": v(-27.02, 58.82) * mm, "radius": 20.32 * mm, "construction": true});
            skCircle(sketch, "E18", {"center": v(27.02, 58.82) * mm, "radius": 20.32 * mm, "construction": true});
            skCircle(sketch, "E19", {"center": v(27.02, 58.82) * mm, "radius": 13.97 * mm});
            skCircle(sketch, "E20", {"center": v(-27.02, 58.82) * mm, "radius": 13.97 * mm});
            skCircle(sketch, "E21", {"center": v(-27.02, 58.82) * mm, "radius": 5.08 * mm});
            skCircle(sketch, "E22", {"center": v(27.02, 58.82) * mm, "radius": 5.08 * mm});
            skSolve(sketch);
        }
        {
            var Q0;
            Q0=qSketchRegion(id+"F7",true);
            extrude(context, id + "F8", {"entities" : qUnion([Q0]), "operationType" : NewBodyOperationType.REMOVE, "oppositeDirection" : true, "depth" : 1.27 * mm});
        }
        {
            var Q0;
            Q0=makeQuery(id+"F6.boolean.opBoolean","COPY",EDGE,{"derivedFrom":makeQuery(id+"F6.opExtrude","CAP_EDGE",EDGE,{"disambiguationData":[OSD([sQuery(id+"F5.wireOp",EDGE,"E15")])],"isStart":true})});
            var Q1;
            Q1=makeQuery(id+"F6.boolean.opBoolean","COPY",EDGE,{"derivedFrom":makeQuery(id+"F6.opExtrude","CAP_EDGE",EDGE,{"disambiguationData":[OSD([sQuery(id+"F5.wireOp",EDGE,"E16")])],"isStart":true})});
            var Q2;
            Q2=makeQuery(id+"F8.boolean.opBoolean","COPY",EDGE,{"derivedFrom":makeQuery(id+"F8.opExtrude","CAP_EDGE",EDGE,{"disambiguationData":[OSD([sQuery(id+"F7.wireOp",EDGE,"E21")])],"isStart":true})});
            var Q3;
            Q3=makeQuery(id+"F8.boolean.opBoolean","COPY",EDGE,{"derivedFrom":makeQuery(id+"F8.opExtrude","CAP_EDGE",EDGE,{"disambiguationData":[OSD([sQuery(id+"F7.wireOp",EDGE,"E22")])],"isStart":true})});
            fillet(context, id + "F9", {"entities" : qUnion([Q0, Q1, Q2, Q3]), "radius" : 1.27 * mm, "tangentPropagation" : true, "allowEdgeOverflow" : false});
        }
        {
            var Q0;
            Q0=qCreatedBy(makeId("Front.planeOp"),FACE);
            var sketch = newSketch(context, id + "F10", { "sketchPlane" : qUnion([Q0])});
            skArc(sketch, "E23.0", {"start": v(7.6, 64.8) * mm, "mid": v(6.7, 58.82) * mm, "end": v(7.6, 52.84) * mm});
            skArc(sketch, "E23.1", {"start": v(-7.6, 52.84) * mm, "mid": v(-6.7, 58.82) * mm, "end": v(-7.6, 64.8) * mm});
            skLineSegment(sketch, "E24", {"start": v(-6.38, 51.2) * mm, "end": v(6.38, 51.2) * mm});
            skLineSegment(sketch, "E25", {"start": v(-6.38, 66.44) * mm, "end": v(6.38, 66.44) * mm});
            skPoint(sketch, "E26.visualSharp", {"position": v(-8.18, 66.44) * mm});
            skArc(sketch, "E26.filletArc", {"start": v(-6.38, 66.44) * mm, "mid": v(-7.4, 65.92) * mm, "end": v(-7.6, 64.8) * mm});
            skPoint(sketch, "E27.visualSharp", {"position": v(8.18, 66.44) * mm});
            skArc(sketch, "E27.filletArc", {"start": v(7.6, 64.8) * mm, "mid": v(7.4, 65.92) * mm, "end": v(6.38, 66.44) * mm});
            skPoint(sketch, "E28.visualSharp", {"position": v(8.18, 51.2) * mm});
            skArc(sketch, "E28.filletArc", {"start": v(6.38, 51.2) * mm, "mid": v(7.4, 51.71) * mm, "end": v(7.6, 52.84) * mm});
            skPoint(sketch, "E29.visualSharp", {"position": v(-8.18, 51.2) * mm});
            skArc(sketch, "E29.filletArc", {"start": v(-7.6, 52.84) * mm, "mid": v(-7.4, 51.71) * mm, "end": v(-6.38, 51.2) * mm});
            skSolve(sketch);
        }
        {
            var Q0;
            Q0=qSketchRegion(id+"F10",true);
            extrude(context, id + "F11", {"entities" : qUnion([Q0]), "depth" : 20.32 * mm});
        }
        {
            var Q0;
            Q0=makeQuery(id+"F11.opExtrude","CAP_FACE",FACE,{"disambiguationData":[OSD([sQuery(id+"F10.wireOp",EDGE,"E23.0"),sQuery(id+"F10.wireOp",EDGE,"E23.1"),sQuery(id+"F10.wireOp",EDGE,"E24"),sQuery(id+"F10.wireOp",EDGE,"E25"),sQuery(id+"F10.wireOp",EDGE,"E26.filletArc"),sQuery(id+"F10.wireOp",EDGE,"E27.filletArc"),sQuery(id+"F10.wireOp",EDGE,"E28.filletArc"),sQuery(id+"F10.wireOp",EDGE,"E29.filletArc")])],"isStart":false});
            var sketch = newSketch(context, id + "F12", { "sketchPlane" : qUnion([Q0])});
            skLineSegment(sketch, "E30.bottom", {"start": v(-5.43, 66.44) * mm, "end": v(5.43, 66.44) * mm});
            skLineSegment(sketch, "E30.top", {"start": v(-5.43, 51.2) * mm, "end": v(5.43, 51.2) * mm});
            skLineSegment(sketch, "E30.left", {"start": v(-5.43, 66.44) * mm, "end": v(-5.43, 51.2) * mm});
            skLineSegment(sketch, "E30.right", {"start": v(5.43, 66.44) * mm, "end": v(5.43, 51.2) * mm});
            skSolve(sketch);
        }
        {
            var Q0;
            Q0=qSketchRegion(id+"F12",true);
            extrude(context, id + "F13", {"entities" : qUnion([Q0]), "operationType" : NewBodyOperationType.REMOVE, "oppositeDirection" : true, "depth" : 8.9 * mm});
        }
        {
            var Q0;
            Q0=makeQuery(id+"F13.boolean.opBoolean","COPY",EDGE,{"derivedFrom":makeQuery(id+"F13.opExtrude","CAP_EDGE",EDGE,{"disambiguationData":[OSD([sQuery(id+"F12.wireOp",EDGE,"E30.left")])],"isStart":false})});
            var Q1;
            Q1=makeQuery(id+"F13.boolean.opBoolean","COPY",EDGE,{"derivedFrom":makeQuery(id+"F13.opExtrude","CAP_EDGE",EDGE,{"disambiguationData":[OSD([sQuery(id+"F12.wireOp",EDGE,"E30.right")])],"isStart":false})});
            fillet(context, id + "F14", {"entities" : qUnion([Q0, Q1]), "radius" : 1.27 * mm, "tangentPropagation" : true, "allowEdgeOverflow" : false});
        }
        {
            var Q0;
            Q0=makeQuery(id+"F13.boolean.opBoolean","COPY",FACE,{"derivedFrom":makeQuery(id+"F13.opExtrude","SWEPT_FACE",FACE,{"disambiguationData":[OSD([sQuery(id+"F12.wireOp",EDGE,"E30.left")])]})});
            var sketch = newSketch(context, id + "F15", { "sketchPlane" : qUnion([Q0])});
            skCircle(sketch, "E31", {"center": v(-16.64, 55.64) * mm, "radius": 1.9 * mm, "construction": true});
            skCircle(sketch, "E32.cCircle", {"center": v(-16.64, 62) * mm, "radius": 1.9 * mm, "construction": true});
            skLineSegment(sketch, "E32.0", {"start": v(-17.74, 63.9) * mm, "end": v(-15.54, 63.9) * mm});
            skLineSegment(sketch, "E32.1", {"start": v(-15.54, 63.9) * mm, "end": v(-14.44, 62) * mm});
            skLineSegment(sketch, "E32.2", {"start": v(-14.44, 62) * mm, "end": v(-15.54, 60.09) * mm});
            skLineSegment(sketch, "E32.3", {"start": v(-15.54, 60.09) * mm, "end": v(-17.74, 60.09) * mm});
            skLineSegment(sketch, "E32.4", {"start": v(-17.74, 60.09) * mm, "end": v(-18.84, 62) * mm});
            skLineSegment(sketch, "E32.5", {"start": v(-18.84, 62) * mm, "end": v(-17.74, 63.9) * mm});
            skPoint(sketch, "E32.0.midPoint", {"position": v(-16.64, 63.9) * mm});
            skLineSegment(sketch, "E33.0", {"start": v(-17.74, 57.55) * mm, "end": v(-15.54, 57.55) * mm});
            skLineSegment(sketch, "E33.1", {"start": v(-15.54, 57.55) * mm, "end": v(-14.44, 55.64) * mm});
            skLineSegment(sketch, "E33.2", {"start": v(-14.44, 55.64) * mm, "end": v(-15.54, 53.74) * mm});
            skLineSegment(sketch, "E33.3", {"start": v(-15.54, 53.74) * mm, "end": v(-17.74, 53.74) * mm});
            skLineSegment(sketch, "E33.4", {"start": v(-17.74, 53.74) * mm, "end": v(-18.84, 55.64) * mm});
            skLineSegment(sketch, "E33.5", {"start": v(-18.84, 55.64) * mm, "end": v(-17.74, 57.55) * mm});
            skPoint(sketch, "E33.0.midPoint", {"position": v(-16.64, 57.55) * mm});
            skSolve(sketch);
        }
        {
            var Q0;
            Q0=qSketchRegion(id+"F15",true);
            extrude(context, id + "F16", {"entities" : qUnion([Q0]), "depth" : 1.52 * mm});
        }
        {
            var Q0;
            Q0=makeQuery(id+"F16.opExtrude","SWEPT_BODY",BODY,{"disambiguationData":[OSD([sQuery(id+"F15.wireOp",EDGE,"E32.0"),sQuery(id+"F15.wireOp",EDGE,"E32.1"),sQuery(id+"F15.wireOp",EDGE,"E32.2"),sQuery(id+"F15.wireOp",EDGE,"E32.3"),sQuery(id+"F15.wireOp",EDGE,"E32.4"),sQuery(id+"F15.wireOp",EDGE,"E32.5")])]});
            var Q1;
            Q1=makeQuery(id+"F16.opExtrude","SWEPT_BODY",BODY,{"disambiguationData":[OSD([sQuery(id+"F15.wireOp",EDGE,"E33.0"),sQuery(id+"F15.wireOp",EDGE,"E33.1"),sQuery(id+"F15.wireOp",EDGE,"E33.2"),sQuery(id+"F15.wireOp",EDGE,"E33.3"),sQuery(id+"F15.wireOp",EDGE,"E33.4"),sQuery(id+"F15.wireOp",EDGE,"E33.5")])]});
            var Q2;
            Q2=qCreatedBy(makeId("Right.planeOp"),FACE);
            mirror(context, id + "F17", {"operationType" : NewBodyOperationType.ADD, "entities" : qUnion([Q0, Q1]), "mirrorPlane" : qUnion([Q2])});
        }
        {
            var Q0;
            Q0=makeQuery(id+"F13.boolean.opBoolean","COPY",FACE,{"derivedFrom":makeQuery(id+"F13.opExtrude","CAP_FACE",FACE,{"disambiguationData":[OSD([sQuery(id+"F12.wireOp",EDGE,"E30.bottom"),sQuery(id+"F12.wireOp",EDGE,"E30.top"),sQuery(id+"F12.wireOp",EDGE,"E30.left"),sQuery(id+"F12.wireOp",EDGE,"E30.right")])],"isStart":false})});
            var sketch = newSketch(context, id + "F18", { "sketchPlane" : qUnion([Q0])});
            skArc(sketch, "E34", {"start": v(-0.25, 61.34) * mm, "mid": v(-1.8, 60.61) * mm, "end": v(-2.53, 59.07) * mm});
            skLineSegment(sketch, "E35.left", {"start": v(-0.25, 61.36) * mm, "end": v(-0.25, 59.07) * mm});
            skLineSegment(sketch, "E35.right", {"start": v(0.25, 61.36) * mm, "end": v(0.25, 59.07) * mm});
            skLineSegment(sketch, "E36.bottom", {"start": v(-2.54, 59.07) * mm, "end": v(-0.25, 59.07) * mm});
            skLineSegment(sketch, "E36.top", {"start": v(-2.54, 58.56) * mm, "end": v(-0.25, 58.56) * mm});
            skLineSegment(sketch, "E37.trimOffspring", {"start": v(0.25, 59.07) * mm, "end": v(2.54, 59.07) * mm});
            skLineSegment(sketch, "E38.trimOffspring", {"start": v(0.25, 58.56) * mm, "end": v(2.54, 58.56) * mm});
            skLineSegment(sketch, "E39.trimOffspring", {"start": v(-0.25, 58.56) * mm, "end": v(-0.25, 56.28) * mm});
            skLineSegment(sketch, "E40.trimOffspring", {"start": v(0.25, 58.56) * mm, "end": v(0.25, 56.28) * mm});
            skArc(sketch, "E41.trimOffspring", {"start": v(-2.53, 58.56) * mm, "mid": v(-1.8, 57.02) * mm, "end": v(-0.25, 56.3) * mm});
            skArc(sketch, "E42.trimOffspring", {"start": v(2.53, 59.07) * mm, "mid": v(1.8, 60.61) * mm, "end": v(0.25, 61.34) * mm});
            skArc(sketch, "E43.trimOffspring", {"start": v(0.25, 56.3) * mm, "mid": v(1.8, 57.02) * mm, "end": v(2.53, 58.56) * mm});
            skSolve(sketch);
        }
        {
            var Q0;
            Q0=qSketchRegion(id+"F18",true);
            extrude(context, id + "F19", {"entities" : qUnion([Q0]), "operationType" : NewBodyOperationType.ADD, "depth" : 0.76 * mm});
        }
        {
            var Q0;
            Q0=makeQuery(id+"F19.opExtrude","CAP_EDGE",EDGE,{"disambiguationData":[OSD([sQuery(id+"F18.wireOp",EDGE,"E42.trimOffspring")])],"isStart":false});
            var Q1;
            Q1=makeQuery(id+"F19.opExtrude","CAP_EDGE",EDGE,{"disambiguationData":[OSD([sQuery(id+"F18.wireOp",EDGE,"E34")])],"isStart":false});
            var Q2;
            Q2=makeQuery(id+"F19.opExtrude","CAP_EDGE",EDGE,{"disambiguationData":[OSD([sQuery(id+"F18.wireOp",EDGE,"E41.trimOffspring")])],"isStart":false});
            var Q3;
            Q3=makeQuery(id+"F19.opExtrude","CAP_EDGE",EDGE,{"disambiguationData":[OSD([sQuery(id+"F18.wireOp",EDGE,"E43.trimOffspring")])],"isStart":false});
            fillet(context, id + "F20", {"entities" : qUnion([Q0, Q1, Q2, Q3]), "radius" : 0.5 * mm, "tangentPropagation" : true, "allowEdgeOverflow" : false});
        }
        {
            var Q0;
            Q0=makeQuery(id+"F11.opExtrude","SWEPT_BODY",BODY,{"disambiguationData":[OSD([sQuery(id+"F10.wireOp",EDGE,"E23.0"),sQuery(id+"F10.wireOp",EDGE,"E23.1"),sQuery(id+"F10.wireOp",EDGE,"E24"),sQuery(id+"F10.wireOp",EDGE,"E25"),sQuery(id+"F10.wireOp",EDGE,"E26.filletArc"),sQuery(id+"F10.wireOp",EDGE,"E27.filletArc"),sQuery(id+"F10.wireOp",EDGE,"E28.filletArc"),sQuery(id+"F10.wireOp",EDGE,"E29.filletArc")])]});
            var Q1;
            Q1=makeQuery(id+"F1.opExtrude","SWEPT_BODY",BODY,{"disambiguationData":[OSD([sQuery(id+"F0.wireOp",EDGE,"E1")])]});
            var Q2;
            Q2=qCreatedBy(makeId("Front.planeOp"),FACE);
            mirror(context, id + "F21", {"operationType" : NewBodyOperationType.ADD, "entities" : qUnion([Q0, Q1]), "mirrorPlane" : qUnion([Q2])});
        }
        {
            var Q0;
            Q0=qCreatedBy(makeId("Front.planeOp"),FACE);
            var sketch = newSketch(context, id + "F22", { "sketchPlane" : qUnion([Q0])});
            skLineSegment(sketch, "E44", {"start": v(0, 58.82) * mm, "end": v(0, 0) * mm, "construction": true});
            skSolve(sketch);
        }
        {
            var Q0;
            Q0=makeQuery(id+"F1.opExtrude","SWEPT_BODY",BODY,{"disambiguationData":[OSD([sQuery(id+"F0.wireOp",EDGE,"E0"),sQuery(id+"F0.wireOp",EDGE,"E2")])]});
            var Q1;
            Q1=sQuery(id+"F22.wireOp",EDGE,"E44");
            transform(context, id + "F23", {"entities" : qUnion([Q0]), "transformType" : TransformType.TRANSLATION_ENTITY, "oppositeDirectionEntity" : false, "transformLine" : qUnion([Q1]), "makeCopy" : false});
        }
    });
